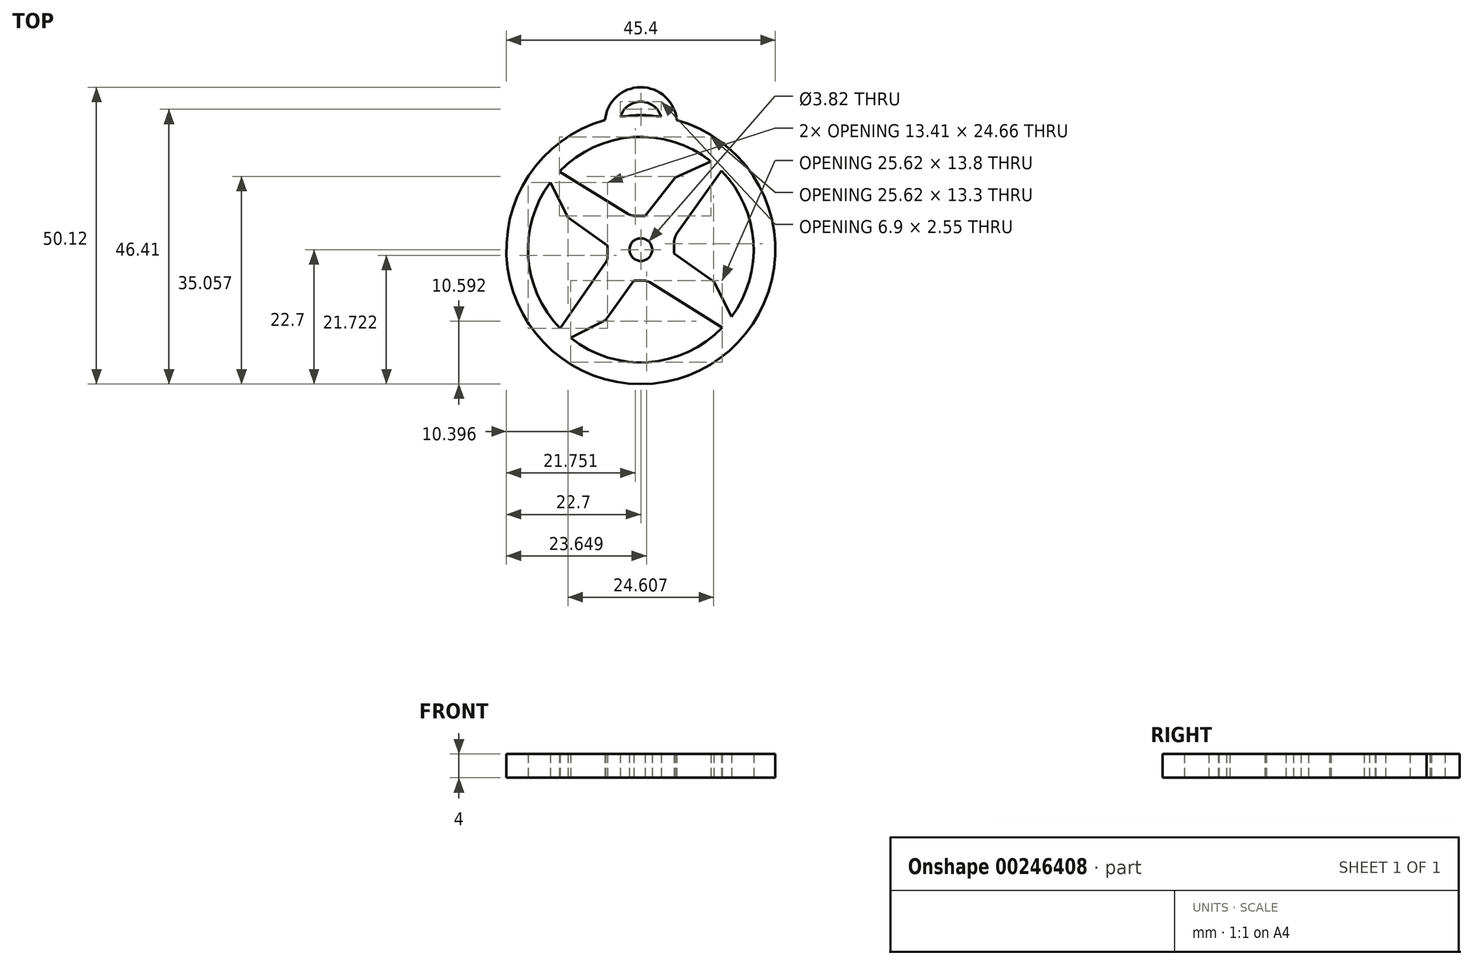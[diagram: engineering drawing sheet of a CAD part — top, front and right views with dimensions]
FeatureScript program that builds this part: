
annotation { "Feature Type Name" : "Feature", "Feature Type Description" : "" }
export const myFeature = defineFeature(function(context is Context, id is Id, definition is map)
    precondition{}
    {
        {
            var Q0;
            Q0=qCreatedBy(makeId("Top.planeOp"),FACE);
            var sketch = newSketch(context, id + "F0", { "sketchPlane" : qUnion([Q0])});
            skLineSegment(sketch, "E0.bottom", {"start": v(0.73, 5.7) * mm, "end": v(-1.04, 5.7) * mm});
            skLineSegment(sketch, "E0.top", {"start": v(0.46, -5.2) * mm, "end": v(-1.16, -5.2) * mm});
            skLineSegment(sketch, "E0.left", {"start": v(5.6, 1.01) * mm, "end": v(5.6, -0.65) * mm});
            skLineSegment(sketch, "E0.right", {"start": v(-5.6, 0.65) * mm, "end": v(-5.6, -1.1) * mm});
            skPoint(sketch, "E0.middle", {"position": v(0, 0) * mm});
            skLineSegment(sketch, "E1", {"start": v(0.73, 5.7) * mm, "end": v(5.82, 12.2) * mm});
            skCircle(sketch, "E2", {"center": v(0, 0) * mm, "radius": 1.91 * mm});
            skLineSegment(sketch, "E3", {"start": v(6.2, 2.91) * mm, "end": v(13.63, 13.3) * mm});
            skLineSegment(sketch, "E4", {"start": v(1.48, -5.5) * mm, "end": v(13.76, -13.18) * mm});
            skLineSegment(sketch, "E5", {"start": v(-5.94, -2.2) * mm, "end": v(-13.63, -13.3) * mm});
            skLineSegment(sketch, "E6", {"start": v(-2.12, 6.01) * mm, "end": v(-13.76, 13.18) * mm});
            skLineSegment(sketch, "E7", {"start": v(5.6, -0.65) * mm, "end": v(12.32, -5.45) * mm});
            skLineSegment(sketch, "E8", {"start": v(-1.16, -5.2) * mm, "end": v(-5.95, -11.92) * mm});
            skLineSegment(sketch, "E9", {"start": v(-5.6, 0.65) * mm, "end": v(-12.32, 5.45) * mm});
            skPoint(sketch, "E10.start.orphan", {"position": v(1.91, 0) * mm});
            skPoint(sketch, "E11.start.orphan", {"position": v(0, -1.91) * mm});
            skPoint(sketch, "E12.start.orphan", {"position": v(-1.91, 0) * mm});
            skPoint(sketch, "E13.start.orphan", {"position": v(0, 1.91) * mm});
            skPoint(sketch, "E14.visualSharp", {"position": v(-1.62, 5.7) * mm});
            skArc(sketch, "E14.filletArc", {"start": v(-2.12, 6.01) * mm, "mid": v(-1.6, 5.79) * mm, "end": v(-1.04, 5.7) * mm});
            skPoint(sketch, "E15.visualSharp", {"position": v(-5.6, -1.7) * mm});
            skArc(sketch, "E15.filletArc", {"start": v(-5.94, -2.2) * mm, "mid": v(-5.69, -1.67) * mm, "end": v(-5.6, -1.1) * mm});
            skPoint(sketch, "E16.visualSharp", {"position": v(5.6, 2.06) * mm});
            skArc(sketch, "E16.filletArc", {"start": v(6.2, 2.91) * mm, "mid": v(5.76, 2.01) * mm, "end": v(5.6, 1.01) * mm});
            skPoint(sketch, "E17.visualSharp", {"position": v(1.01, -5.2) * mm});
            skArc(sketch, "E17.filletArc", {"start": v(1.48, -5.5) * mm, "mid": v(1, -5.28) * mm, "end": v(0.46, -5.2) * mm});
            skLineSegment(sketch, "E18.bottom", {"start": v(-25.4, 27.6) * mm, "end": v(25.4, 27.6) * mm});
            skLineSegment(sketch, "E18.top", {"start": v(-25.4, -23.2) * mm, "end": v(25.4, -23.2) * mm});
            skLineSegment(sketch, "E18.left", {"start": v(-25.4, 27.6) * mm, "end": v(-25.4, -23.2) * mm});
            skLineSegment(sketch, "E18.right", {"start": v(25.4, 27.6) * mm, "end": v(25.4, -23.2) * mm});
            skCircle(sketch, "E19", {"center": v(0, 0) * mm, "radius": 19.05 * mm});
            skCircle(sketch, "E20", {"center": v(0, 0) * mm, "radius": 22.7 * mm});
            skArc(sketch, "E21", {"start": v(3.45, 22.43) * mm, "mid": v(0, 24.99) * mm, "end": v(-3.45, 22.43) * mm});
            skArc(sketch, "E22", {"start": v(6.05, 21.87) * mm, "mid": v(0, 27.42) * mm, "end": v(-6.05, 21.87) * mm});
            skLineSegment(sketch, "E23", {"start": v(-12.32, 5.45) * mm, "end": v(-15.3, 11.35) * mm});
            skLineSegment(sketch, "E24", {"start": v(5.82, 12.2) * mm, "end": v(11.86, 14.9) * mm});
            skLineSegment(sketch, "E25", {"start": v(12.32, -5.45) * mm, "end": v(15.3, -11.35) * mm});
            skLineSegment(sketch, "E26", {"start": v(-5.95, -11.92) * mm, "end": v(-11.86, -14.9) * mm});
            skSolve(sketch);
        }
        {
            var Q0;
            Q0=makeQuery(id+"F0.imprint","IMPRINT",FACE,{"disambiguationData":[TD([[makeQuery(id+"F0.imprint","IMPRINT",EDGE,{"derivedFrom":sQuery(id+"F0.wireOp",EDGE,"E0.bottom")}),1.0]])]});
            var Q1;
            {var subQ3=sQuery(id+"F0.wireOp",EDGE,"E21");var subQ4=sQuery(id+"F0.wireOp",EDGE,"E20");var subQ5=makeQuery(id+"F0.imprint","INTERSECT",VERTEX,{"disambiguationData":[OD(0.0)],"derivedFrom":[subQ4,subQ3]});Q1=makeQuery(id+"F0.imprint","IMPRINT",FACE,{"disambiguationData":[TD([[makeQuery(id+"F0.imprint","IMPRINT",EDGE,{"disambiguationData":[TD([[subQ5,-1.0]])],"derivedFrom":subQ4}),1.0]])]});}
            var Q2;
            {var subQ0=sQuery(id+"F0.wireOp",EDGE,"E21");Q2=makeQuery(id+"F0.imprint","IMPRINT",FACE,{"disambiguationData":[TD([[makeQuery(id+"F0.imprint","IMPRINT",EDGE,{"derivedFrom":subQ0}),-1.0]])]});}
            extrude(context, id + "F1", {"entities" : qUnion([Q0, Q1, Q2]), "depth" : 4 * mm});
        }
    });
